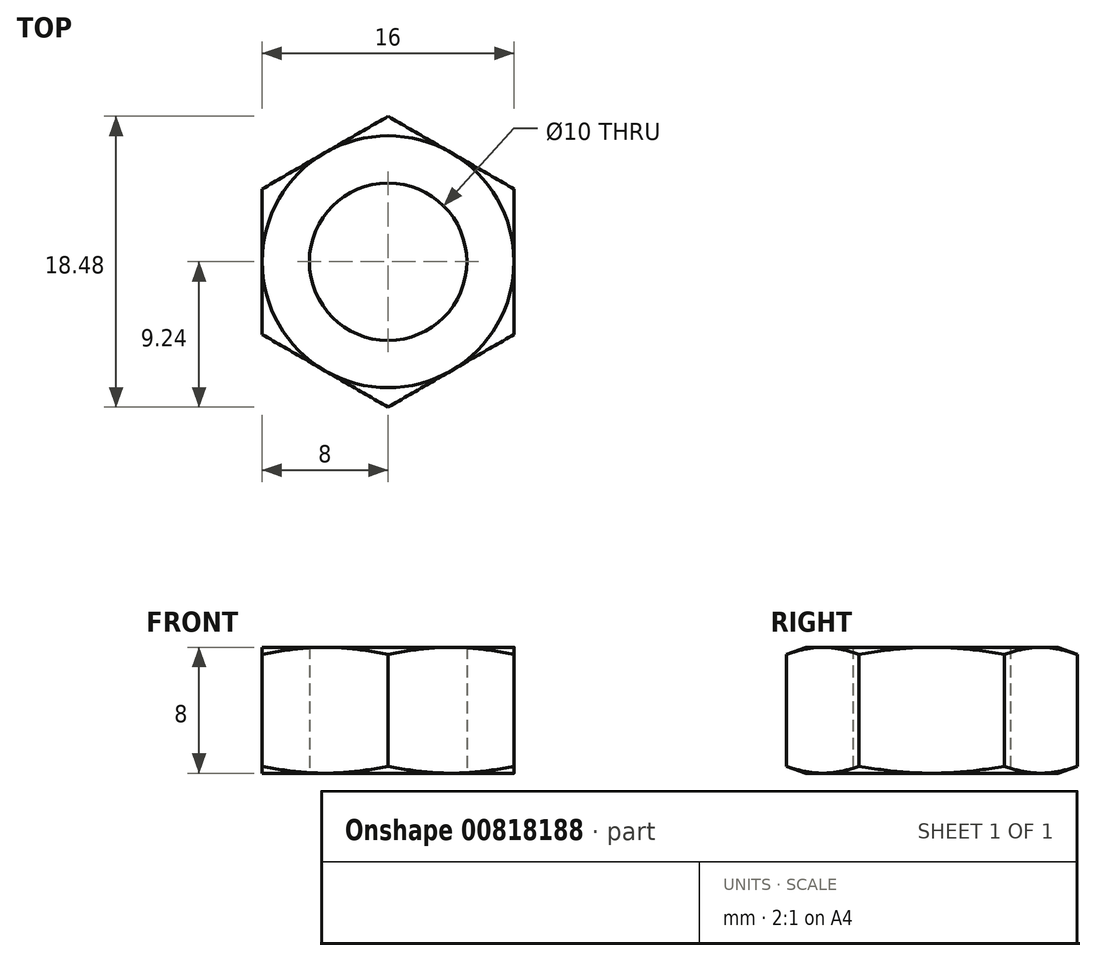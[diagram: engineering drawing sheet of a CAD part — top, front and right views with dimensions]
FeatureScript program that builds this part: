
annotation { "Feature Type Name" : "Feature", "Feature Type Description" : "" }
export const myFeature = defineFeature(function(context is Context, id is Id, definition is map)
    precondition{}
    {
        {
            var Q0;
            Q0=qCreatedBy(makeId("Top.planeOp"),FACE);
            var sketch = newSketch(context, id + "F0", { "sketchPlane" : qUnion([Q0])});
            skCircle(sketch, "E0", {"center": v(0, 0) * mm, "radius": 5 * mm});
            skCircle(sketch, "E1.cCircle", {"center": v(0, 0) * mm, "radius": 8 * mm, "construction": true});
            skLineSegment(sketch, "E1.0", {"start": v(8, 4.62) * mm, "end": v(8, -4.62) * mm});
            skLineSegment(sketch, "E1.1", {"start": v(8, -4.62) * mm, "end": v(0, -9.24) * mm});
            skLineSegment(sketch, "E1.2", {"start": v(0, -9.24) * mm, "end": v(-8, -4.62) * mm});
            skLineSegment(sketch, "E1.3", {"start": v(-8, -4.62) * mm, "end": v(-8, 4.62) * mm});
            skLineSegment(sketch, "E1.4", {"start": v(-8, 4.62) * mm, "end": v(0, 9.24) * mm});
            skLineSegment(sketch, "E1.5", {"start": v(0, 9.24) * mm, "end": v(8, 4.62) * mm});
            skPoint(sketch, "E1.0.midPoint", {"position": v(8, 0) * mm});
            skSolve(sketch);
        }
        {
            var Q0;
            Q0=makeQuery(id+"F0.imprint","IMPRINT",FACE,{"disambiguationData":[TD([[makeQuery(id+"F0.imprint","IMPRINT",EDGE,{"derivedFrom":sQuery(id+"F0.wireOp",EDGE,"E0")}),-1.0]])]});
            extrude(context, id + "F1", {"entities" : qUnion([Q0]), "depth" : 8 * mm, "offsetDistance" : 25 * mm});
        }
        {
            var Q0;
            Q0=qCreatedBy(makeId("Right.planeOp"),FACE);
            var sketch = newSketch(context, id + "F2", { "sketchPlane" : qUnion([Q0])});
            skLineSegment(sketch, "E2", {"start": v(0, 0) * mm, "end": v(-8, 0) * mm});
            skLineSegment(sketch, "E3", {"start": v(-8, 0) * mm, "end": v(-9.24, 0.45) * mm});
            skLineSegment(sketch, "E4", {"start": v(-9.24, 0.45) * mm, "end": v(-9.24, 7.55) * mm});
            skLineSegment(sketch, "E5", {"start": v(-9.24, 7.55) * mm, "end": v(-8, 8) * mm});
            skLineSegment(sketch, "E6", {"start": v(-8, 8) * mm, "end": v(0, 8) * mm});
            skLineSegment(sketch, "E7", {"start": v(0, 8) * mm, "end": v(0, 0) * mm});
            skLineSegment(sketch, "E8", {"start": v(0, -2.45) * mm, "end": v(0, 11.92) * mm, "construction": true});
            skSolve(sketch);
        }
        {
            var Q0;
            Q0 = qSketchRegion(id + "F2", true);
            var Q1;
            Q1=sQuery(id+"F2.wireOp",EDGE,"E8");
            revolve(context, id + "F3", {"operationType" : NewBodyOperationType.INTERSECT, "surfaceOperationType" : NewSurfaceOperationType.NEW, "entities" : qUnion([Q0]), "axis" : qUnion([Q1]), "revolveType" : RevolveType.FULL});
        }
    });
